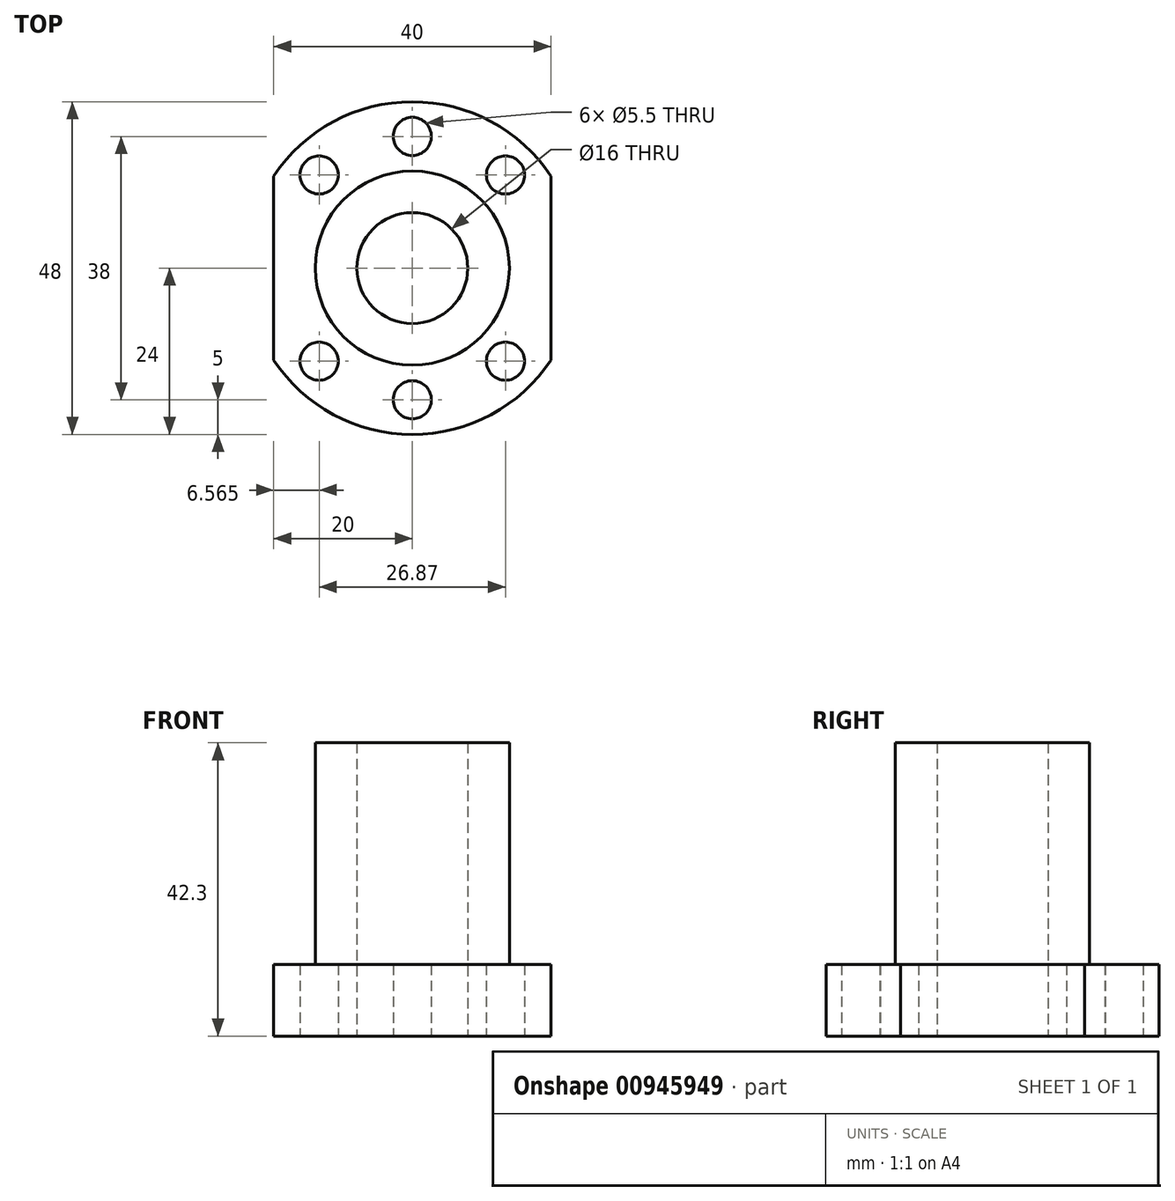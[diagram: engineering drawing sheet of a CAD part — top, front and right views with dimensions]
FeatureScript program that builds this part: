
annotation { "Feature Type Name" : "Feature", "Feature Type Description" : "" }
export const myFeature = defineFeature(function(context is Context, id is Id, definition is map)
    precondition{}
    {
        {
            var Q0;
            Q0=qCreatedBy(makeId("Top.planeOp"),FACE);
            var sketch = newSketch(context, id + "F0", { "sketchPlane" : qUnion([Q0])});
            skArc(sketch, "E0", {"start": v(-20, -13.27) * mm, "mid": v(0, -24) * mm, "end": v(20, -13.27) * mm});
            skCircle(sketch, "E1", {"center": v(0, 0) * mm, "radius": 14 * mm});
            skCircle(sketch, "E2", {"center": v(0, 0) * mm, "radius": 19 * mm, "construction": true});
            skLineSegment(sketch, "E3", {"start": v(0, 0) * mm, "end": v(0, 24) * mm, "construction": true});
            skLineSegment(sketch, "E4", {"start": v(-20, 13.27) * mm, "end": v(-20, -13.27) * mm});
            skLineSegment(sketch, "E5.MirrorCS", {"start": v(20, 13.27) * mm, "end": v(20, -13.27) * mm});
            skArc(sketch, "E6.trimOffspring", {"start": v(20, 13.27) * mm, "mid": v(0, 24) * mm, "end": v(-20, 13.27) * mm});
            skCircle(sketch, "E7", {"center": v(0, 19) * mm, "radius": 2.75 * mm});
            skCircle(sketch, "E8", {"center": v(-13.44, 13.44) * mm, "radius": 2.75 * mm});
            skLineSegment(sketch, "E9", {"start": v(-13.44, 13.44) * mm, "end": v(0, 0) * mm, "construction": true});
            skCircle(sketch, "E10.MirrorC", {"center": v(13.44, 13.44) * mm, "radius": 2.75 * mm});
            skLineSegment(sketch, "E11", {"start": v(-20, 0) * mm, "end": v(20, 0) * mm, "construction": true});
            skCircle(sketch, "E12.MirrorC", {"center": v(13.44, -13.44) * mm, "radius": 2.75 * mm});
            skCircle(sketch, "E13.MirrorC", {"center": v(-13.44, -13.44) * mm, "radius": 2.75 * mm});
            skCircle(sketch, "E14.MirrorC", {"center": v(0, -19) * mm, "radius": 2.75 * mm});
            skCircle(sketch, "E15", {"center": v(0, 0) * mm, "radius": 8 * mm});
            skSolve(sketch);
        }
        {
            var Q0;
            Q0=makeQuery(id+"F0.imprint","IMPRINT",FACE,{"disambiguationData":[TD([[makeQuery(id+"F0.imprint","IMPRINT",EDGE,{"derivedFrom":sQuery(id+"F0.wireOp",EDGE,"E0")}),1.0]])]});
            var Q1;
            Q1=makeQuery(id+"F0.imprint","IMPRINT",FACE,{"disambiguationData":[TD([[makeQuery(id+"F0.imprint","IMPRINT",EDGE,{"derivedFrom":sQuery(id+"F0.wireOp",EDGE,"E1")}),1.0]])]});
            extrude(context, id + "F1", {"entities" : qUnion([Q0, Q1]), "depth" : 10.3 * mm, "offsetDistance" : 25 * mm});
        }
        {
            var Q0;
            Q0=makeQuery(id+"F0.imprint","IMPRINT",FACE,{"disambiguationData":[TD([[makeQuery(id+"F0.imprint","IMPRINT",EDGE,{"derivedFrom":sQuery(id+"F0.wireOp",EDGE,"E1")}),1.0]])]});
            extrude(context, id + "F2", {"entities" : qUnion([Q0]), "operationType" : NewBodyOperationType.ADD, "depth" : 42.3 * mm, "offsetDistance" : 25 * mm});
        }
    });
